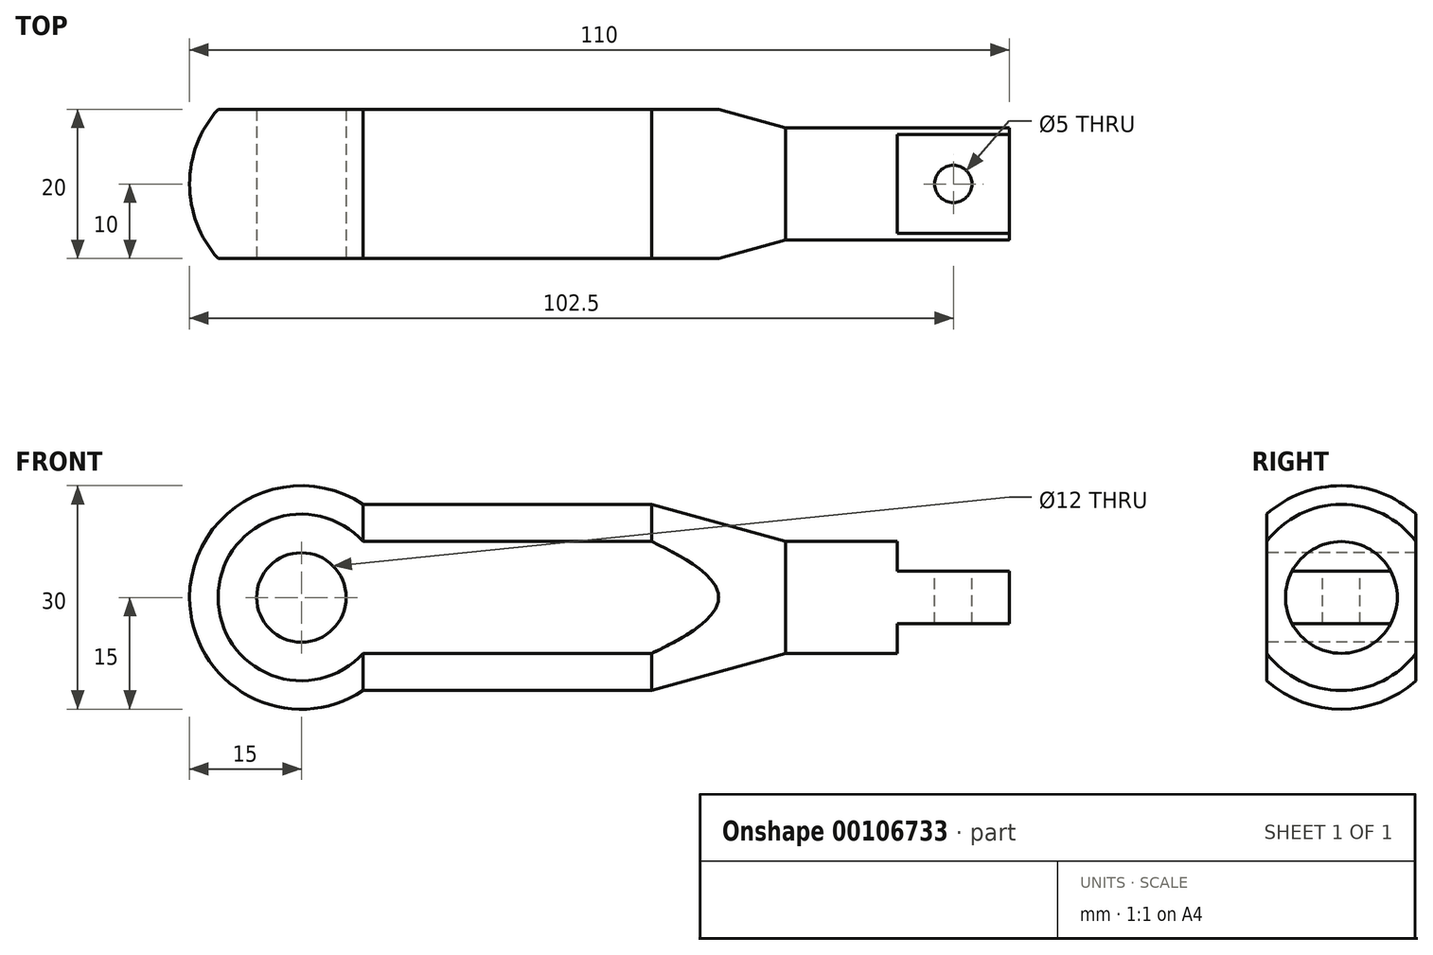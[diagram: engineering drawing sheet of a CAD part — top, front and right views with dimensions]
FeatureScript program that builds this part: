
annotation { "Feature Type Name" : "Feature", "Feature Type Description" : "" }
export const myFeature = defineFeature(function(context is Context, id is Id, definition is map)
    precondition{}
    {
        {
            var Q0;
            Q0=qCreatedBy(makeId("Front.planeOp"),FACE);
            var sketch = newSketch(context, id + "F0", { "sketchPlane" : qUnion([Q0])});
            skArc(sketch, "E0", {"start": v(-15, 0) * mm, "mid": v(-7.1, 13.22) * mm, "end": v(8.3, 12.5) * mm});
            skLineSegment(sketch, "E1", {"start": v(8.3, 12.5) * mm, "end": v(47, 12.5) * mm});
            skLineSegment(sketch, "E2", {"start": v(47, 12.5) * mm, "end": v(65, 7.5) * mm});
            skLineSegment(sketch, "E3", {"start": v(65, 7.5) * mm, "end": v(95, 7.5) * mm});
            skLineSegment(sketch, "E4", {"start": v(95, 7.5) * mm, "end": v(95, 0) * mm});
            skLineSegment(sketch, "E5", {"start": v(95, 0) * mm, "end": v(-15, 0) * mm});
            skLineSegment(sketch, "E6", {"start": v(0, 0) * mm, "end": v(88.94, 0) * mm, "construction": true});
            skSolve(sketch);
        }
        {
            var Q0;
            Q0 = qSketchRegion(id + "F0", true);
            var Q1;
            Q1=sQuery(id+"F0.wireOp",EDGE,"E5");
            revolve(context, id + "F1", {"entities" : qUnion([Q0]), "axis" : qUnion([Q1]), "revolveType" : RevolveType.FULL});
        }
        {
            var Q0;
            Q0=qCreatedBy(makeId("Front.planeOp"),FACE);
            var sketch = newSketch(context, id + "F2", { "sketchPlane" : qUnion([Q0])});
            skLineSegment(sketch, "E7.top", {"start": v(80, 3.5) * mm, "end": v(95, 3.5) * mm});
            skLineSegment(sketch, "E7.left", {"start": v(80, 7.5) * mm, "end": v(80, 3.5) * mm});
            skLineSegment(sketch, "E8", {"start": v(65, 7.5) * mm, "end": v(95, 7.5) * mm});
            skLineSegment(sketch, "E9", {"start": v(80, 7.5) * mm, "end": v(95, 7.5) * mm});
            skLineSegment(sketch, "E10", {"start": v(95, 3.5) * mm, "end": v(95, 7.5) * mm});
            skLineSegment(sketch, "E11", {"start": v(70.46, 0) * mm, "end": v(96.85, 0) * mm, "construction": true});
            skLineSegment(sketch, "E12.MirrorCS", {"start": v(80, -3.5) * mm, "end": v(95, -3.5) * mm});
            skLineSegment(sketch, "E13.MirrorCS", {"start": v(80, -7.5) * mm, "end": v(80, -3.5) * mm});
            skLineSegment(sketch, "E14.MirrorCS", {"start": v(95, -3.5) * mm, "end": v(95, -7.5) * mm});
            skLineSegment(sketch, "E15.MirrorCS", {"start": v(80, -7.5) * mm, "end": v(95, -7.5) * mm});
            skSolve(sketch);
        }
        {
            var Q0;
            Q0 = qSketchRegion(id + "F2", true);
            extrude(context, id + "F3", {"entities" : qUnion([Q0]), "operationType" : NewBodyOperationType.REMOVE, "endBound" : BoundingType.THROUGH_ALL, "oppositeDirection" : true, "depth" : 25 * mm, "hasSecondDirection" : true, "secondDirectionBound" : SecondDirectionBoundingType.THROUGH_ALL, "secondDirectionOppositeDirection" : false, "secondDirectionDepth" : 25 * mm});
        }
        {
            var Q0;
            Q0=makeQuery(id+"F1.opRevolve","SWEPT_FACE",FACE,{"disambiguationData":[OSD([sQuery(id+"F0.wireOp",EDGE,"E4")])]});
            var sketch = newSketch(context, id + "F4", { "sketchPlane" : qUnion([Q0])});
            skArc(sketch, "E16", {"start": v(-10, 11.18) * mm, "mid": v(-15, 0) * mm, "end": v(-10, -11.18) * mm});
            skLineSegment(sketch, "E17", {"start": v(-10, 11.18) * mm, "end": v(-10, -11.18) * mm});
            skLineSegment(sketch, "E18", {"start": v(10, -11.18) * mm, "end": v(10, 11.18) * mm});
            skLineSegment(sketch, "E19", {"start": v(0, 0) * mm, "end": v(0, 20.53) * mm, "construction": true});
            skArc(sketch, "E20.trimOffspring", {"start": v(10, -11.18) * mm, "mid": v(15, 0) * mm, "end": v(10, 11.18) * mm});
            skSolve(sketch);
        }
        {
            var Q0;
            Q0 = qSketchRegion(id + "F4", true);
            extrude(context, id + "F5", {"entities" : qUnion([Q0]), "operationType" : NewBodyOperationType.REMOVE, "endBound" : BoundingType.THROUGH_ALL, "oppositeDirection" : true, "depth" : 25 * mm});
        }
        {
            var Q0;
            Q0=makeQuery(id+"F5.boolean.opBoolean","COPY",FACE,{"derivedFrom":makeQuery(id+"F5.opExtrude","SWEPT_FACE",FACE,{"disambiguationData":[OSD([sQuery(id+"F4.wireOp",EDGE,"E17")])]})});
            var sketch = newSketch(context, id + "F6", { "sketchPlane" : qUnion([Q0])});
            skCircle(sketch, "E21", {"center": v(0, 0) * mm, "radius": 6 * mm});
            skSolve(sketch);
        }
        {
            var Q0;
            Q0 = qSketchRegion(id + "F6", true);
            extrude(context, id + "F7", {"entities" : qUnion([Q0]), "operationType" : NewBodyOperationType.REMOVE, "endBound" : BoundingType.THROUGH_ALL, "oppositeDirection" : true, "depth" : 25 * mm});
        }
        {
            var Q0;
            Q0=makeQuery(id+"F3.boolean.opBoolean","COPY",FACE,{"derivedFrom":makeQuery(id+"F3.opExtrude","SWEPT_FACE",FACE,{"disambiguationData":[OSD([sQuery(id+"F2.wireOp",EDGE,"E7.top")])]})});
            var sketch = newSketch(context, id + "F8", { "sketchPlane" : qUnion([Q0])});
            skCircle(sketch, "E22", {"center": v(87.5, 0) * mm, "radius": 2.5 * mm});
            skSolve(sketch);
        }
        {
            var Q0;
            Q0 = qSketchRegion(id + "F8", true);
            extrude(context, id + "F9", {"entities" : qUnion([Q0]), "operationType" : NewBodyOperationType.REMOVE, "endBound" : BoundingType.THROUGH_ALL, "oppositeDirection" : true, "depth" : 25 * mm});
        }
    });
